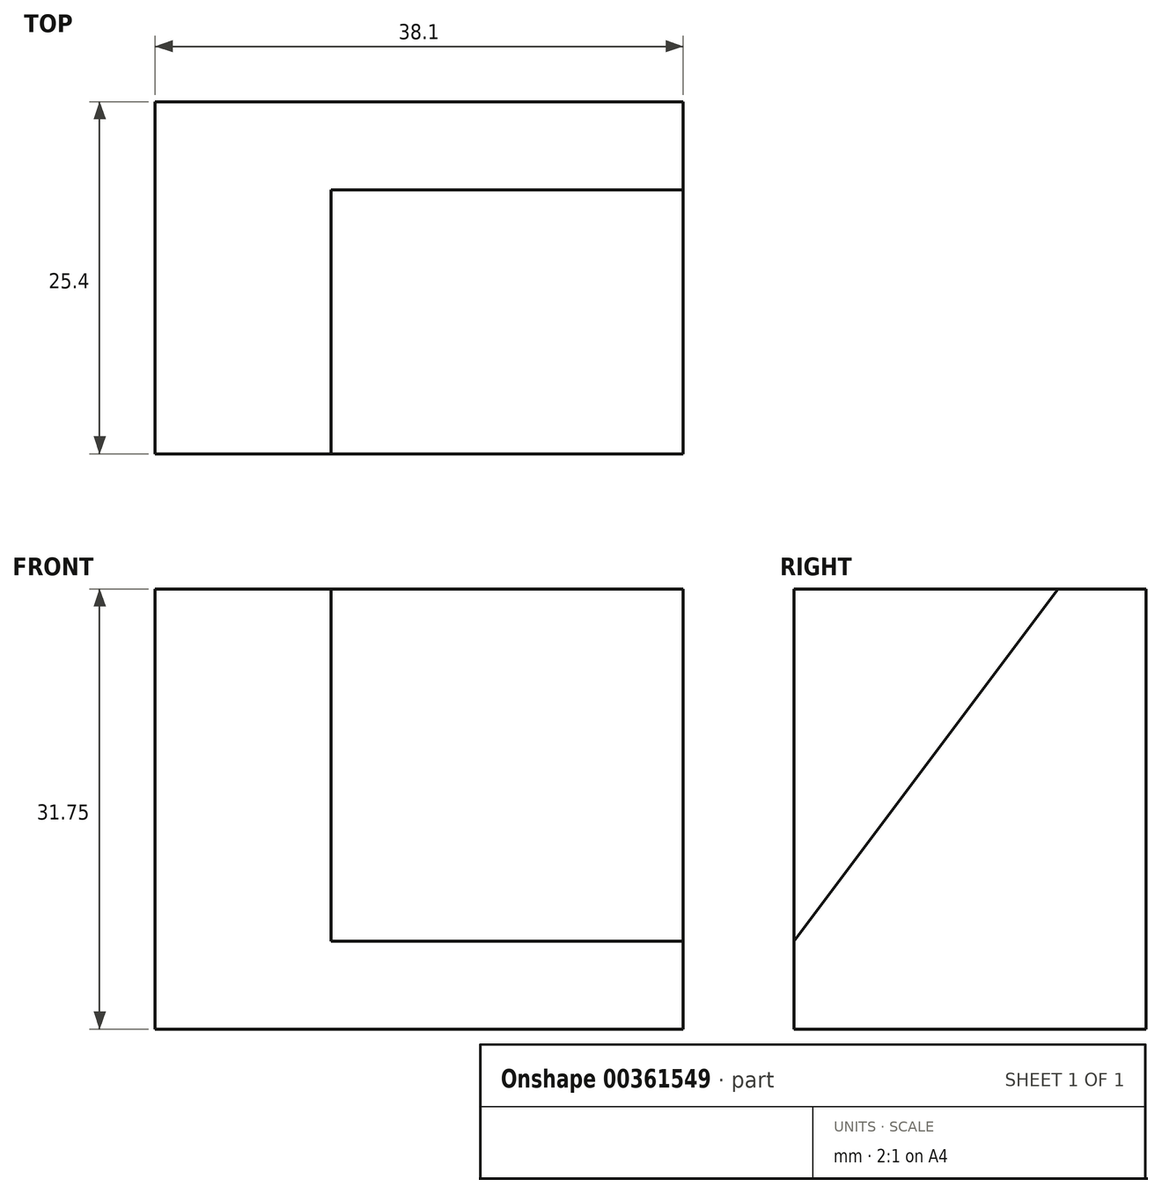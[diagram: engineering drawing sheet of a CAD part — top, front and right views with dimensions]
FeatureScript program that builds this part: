
annotation { "Feature Type Name" : "Feature", "Feature Type Description" : "" }
export const myFeature = defineFeature(function(context is Context, id is Id, definition is map)
    precondition{}
    {
        {
            var Q0;
            Q0=qCreatedBy(makeId("Right.planeOp"),FACE);
            var sketch = newSketch(context, id + "F0", { "sketchPlane" : qUnion([Q0])});
            skLineSegment(sketch, "E0", {"start": v(31.35, 31.75) * mm, "end": v(37.7, 31.75) * mm});
            skLineSegment(sketch, "E1", {"start": v(37.7, 31.75) * mm, "end": v(37.7, 0) * mm});
            skLineSegment(sketch, "E2", {"start": v(37.7, 0) * mm, "end": v(12.3, 0) * mm});
            skLineSegment(sketch, "E3", {"start": v(12.3, 0) * mm, "end": v(12.3, 6.35) * mm});
            skLineSegment(sketch, "E4", {"start": v(12.3, 6.35) * mm, "end": v(31.35, 31.75) * mm});
            skSolve(sketch);
        }
        {
            var Q0;
            Q0 = qSketchRegion(id + "F0", true);
            extrude(context, id + "F1", {"entities" : qUnion([Q0]), "depth" : 38.1 * mm});
        }
        {
            var Q0;
            Q0=makeQuery(id+"F1.opExtrude","CAP_FACE",FACE,{"disambiguationData":[OSD([sQuery(id+"F0.wireOp",EDGE,"E0"),sQuery(id+"F0.wireOp",EDGE,"E1"),sQuery(id+"F0.wireOp",EDGE,"E2"),sQuery(id+"F0.wireOp",EDGE,"E3"),sQuery(id+"F0.wireOp",EDGE,"E4")])],"isStart":true});
            var sketch = newSketch(context, id + "F2", { "sketchPlane" : qUnion([Q0])});
            skLineSegment(sketch, "E5", {"start": v(-37.7, 31.75) * mm, "end": v(-37.7, 0) * mm});
            skLineSegment(sketch, "E6", {"start": v(-37.7, 0) * mm, "end": v(-12.3, 0) * mm});
            skLineSegment(sketch, "E7", {"start": v(-12.3, 0) * mm, "end": v(-12.3, 31.75) * mm});
            skLineSegment(sketch, "E8", {"start": v(-37.7, 31.75) * mm, "end": v(-12.3, 31.75) * mm});
            skSolve(sketch);
        }
        {
            var Q0;
            Q0 = qSketchRegion(id + "F2", true);
            extrude(context, id + "F3", {"entities" : qUnion([Q0]), "operationType" : NewBodyOperationType.ADD, "oppositeDirection" : true, "depth" : 12.7 * mm});
        }
    });
